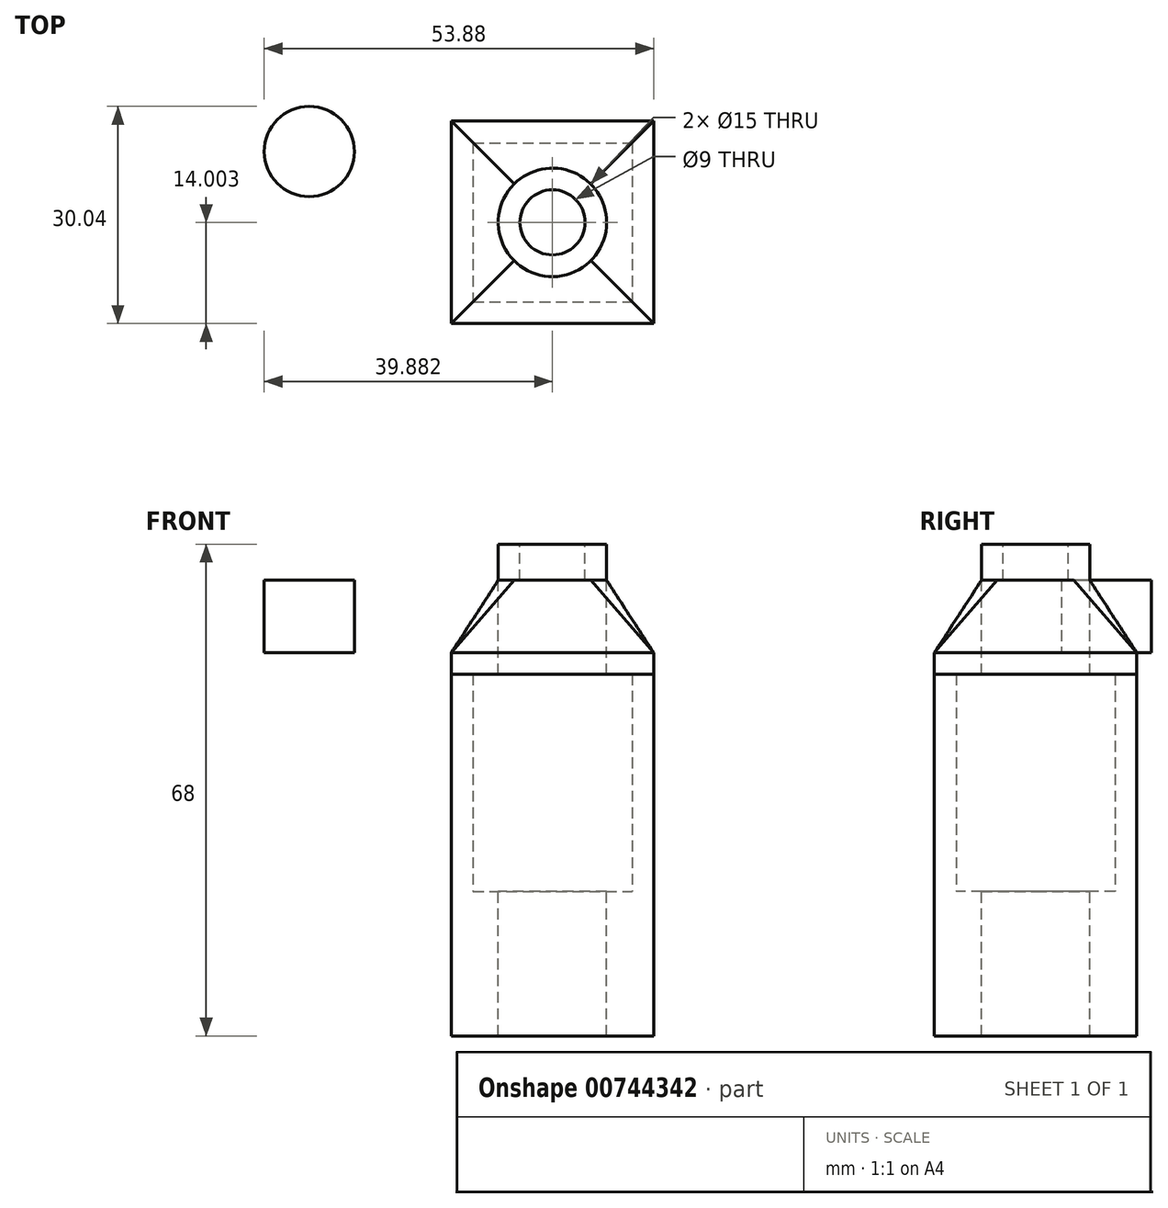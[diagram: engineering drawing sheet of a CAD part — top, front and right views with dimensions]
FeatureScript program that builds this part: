
annotation { "Feature Type Name" : "Feature", "Feature Type Description" : "" }
export const myFeature = defineFeature(function(context is Context, id is Id, definition is map)
    precondition{}
    {
        {
            var Q0;
            Q0=qCreatedBy(makeId("Top.planeOp"),FACE);
            var sketch = newSketch(context, id + "F0", { "sketchPlane" : qUnion([Q0])});
            skLineSegment(sketch, "E0.bottom", {"start": v(-35.87, 27.62) * mm, "end": v(-7.87, 27.62) * mm});
            skLineSegment(sketch, "E0.top", {"start": v(-35.87, -0.38) * mm, "end": v(-7.87, -0.38) * mm});
            skLineSegment(sketch, "E0.left", {"start": v(-35.87, 27.62) * mm, "end": v(-35.87, -0.38) * mm});
            skLineSegment(sketch, "E0.right", {"start": v(-7.87, 27.62) * mm, "end": v(-7.87, -0.38) * mm});
            skLineSegment(sketch, "E1.bottom", {"start": v(-32.87, 24.62) * mm, "end": v(-10.87, 24.62) * mm});
            skLineSegment(sketch, "E1.top", {"start": v(-32.87, 2.62) * mm, "end": v(-10.87, 2.62) * mm});
            skLineSegment(sketch, "E1.left", {"start": v(-32.87, 24.62) * mm, "end": v(-32.87, 2.62) * mm});
            skLineSegment(sketch, "E1.right", {"start": v(-10.87, 24.62) * mm, "end": v(-10.87, 2.62) * mm});
            skSolve(sketch);
        }
        {
            var Q0;
            Q0=makeQuery(id+"F0.imprint","IMPRINT",FACE,{"disambiguationData":[TD([[makeQuery(id+"F0.imprint","IMPRINT",EDGE,{"derivedFrom":sQuery(id+"F0.wireOp",EDGE,"E0.bottom")}),-1.0]])]});
            extrude(context, id + "F1", {"entities" : qUnion([Q0]), "depth" : 50 * mm, "offsetDistance" : 25 * mm});
        }
        {
            var Q0;
            Q0=makeQuery(id+"F0.imprint","IMPRINT",FACE,{"disambiguationData":[TD([[makeQuery(id+"F0.imprint","IMPRINT",EDGE,{"derivedFrom":sQuery(id+"F0.wireOp",EDGE,"E1.bottom")}),-1.0]])]});
            extrude(context, id + "F2", {"entities" : qUnion([Q0]), "operationType" : NewBodyOperationType.ADD, "depth" : 20 * mm, "offsetDistance" : 25 * mm});
        }
        {
            var Q0;
            Q0=makeQuery(id+"F1.opExtrude","CAP_FACE",FACE,{"disambiguationData":[OSD([sQuery(id+"F0.wireOp",EDGE,"E0.bottom"),sQuery(id+"F0.wireOp",EDGE,"E0.top"),sQuery(id+"F0.wireOp",EDGE,"E0.left"),sQuery(id+"F0.wireOp",EDGE,"E0.right"),sQuery(id+"F0.wireOp",EDGE,"E1.bottom"),sQuery(id+"F0.wireOp",EDGE,"E1.top"),sQuery(id+"F0.wireOp",EDGE,"E1.left"),sQuery(id+"F0.wireOp",EDGE,"E1.right")])],"isStart":false});
            var sketch = newSketch(context, id + "F3", { "sketchPlane" : qUnion([Q0])});
            skLineSegment(sketch, "E2.bottom", {"start": v(-35.87, 27.62) * mm, "end": v(-7.87, 27.62) * mm});
            skLineSegment(sketch, "E2.top", {"start": v(-35.87, -0.38) * mm, "end": v(-7.87, -0.38) * mm});
            skLineSegment(sketch, "E2.left", {"start": v(-35.87, 27.62) * mm, "end": v(-35.87, -0.38) * mm});
            skLineSegment(sketch, "E2.right", {"start": v(-7.87, 27.62) * mm, "end": v(-7.87, -0.38) * mm});
            skSolve(sketch);
        }
        {
            var Q0;
            Q0=makeQuery(id+"F3.imprint","IMPRINT",FACE,{"disambiguationData":[TD([[makeQuery(id+"F3.imprint","IMPRINT",EDGE,{"derivedFrom":makeQuery(id+"F1.opExtrude","CAP_EDGE",EDGE,{"disambiguationData":[OSD([sQuery(id+"F0.wireOp",EDGE,"E1.bottom")])],"isStart":false})}),-1.0]])]});
            var Q1;
            Q1=makeQuery(id+"F3.imprint","IMPRINT",FACE,{"disambiguationData":[TD([[makeQuery(id+"F3.imprint","IMPRINT",EDGE,{"derivedFrom":sQuery(id+"F3.wireOp",EDGE,"E2.bottom")}),-1.0]])]});
            extrude(context, id + "F4", {"entities" : qUnion([Q0, Q1]), "depth" : 3 * mm, "offsetDistance" : 25 * mm});
        }
        {
            var Q0;
            Q0=makeQuery(id+"F4.opExtrude","CAP_FACE",FACE,{"disambiguationData":[OSD([sQuery(id+"F3.wireOp",EDGE,"E2.bottom"),sQuery(id+"F3.wireOp",EDGE,"E2.top"),sQuery(id+"F3.wireOp",EDGE,"E2.left"),sQuery(id+"F3.wireOp",EDGE,"E2.right")])],"isStart":false});
            var sketch = newSketch(context, id + "F5", { "sketchPlane" : qUnion([Q0])});
            skCircle(sketch, "E3", {"center": v(-55.52, 23.42) * mm, "radius": 6.24 * mm});
            skSolve(sketch);
        }
        {
            var Q0;
            Q0=makeQuery(id+"F5.imprint","IMPRINT",FACE,{"disambiguationData":[TD([[makeQuery(id+"F5.imprint","IMPRINT",EDGE,{"derivedFrom":sQuery(id+"F5.wireOp",EDGE,"E3")}),1.0]])]});
            extrude(context, id + "F6", {"entities" : qUnion([Q0]), "depth" : 10 * mm, "offsetDistance" : 25 * mm});
        }
        {
            var Q0;
            Q0=makeQuery(id+"F6.opExtrude","CAP_FACE",FACE,{"disambiguationData":[OSD([sQuery(id+"F5.wireOp",EDGE,"E3")])],"isStart":false});
            var sketch = newSketch(context, id + "F7", { "sketchPlane" : qUnion([Q0])});
            skCircle(sketch, "E4", {"center": v(-21.87, 13.62) * mm, "radius": 7.5 * mm});
            skSolve(sketch);
        }
        {
            var Q0;
            Q0=makeQuery(id+"F7.imprint","IMPRINT",FACE,{"disambiguationData":[TD([[makeQuery(id+"F7.imprint","IMPRINT",EDGE,{"derivedFrom":sQuery(id+"F7.wireOp",EDGE,"E4")}),1.0]])]});
            extrude(context, id + "F8", {"entities" : qUnion([Q0]), "depth" : 5 * mm, "offsetDistance" : 25 * mm});
        }
        {
            var Q1;
            Q1=makeQuery(id+"F8.opExtrude","CAP_FACE",FACE,{"disambiguationData":[OSD([sQuery(id+"F7.wireOp",EDGE,"E4")])],"isStart":true});
            var Q2;
            Q2=makeQuery(id+"F4.opExtrude","CAP_FACE",FACE,{"disambiguationData":[OSD([sQuery(id+"F3.wireOp",EDGE,"E2.bottom"),sQuery(id+"F3.wireOp",EDGE,"E2.top"),sQuery(id+"F3.wireOp",EDGE,"E2.left"),sQuery(id+"F3.wireOp",EDGE,"E2.right")])],"isStart":false});
            loft(context, id + "F9", {"operationType" : NewBodyOperationType.ADD, "sheetProfilesArray" : [{ "sheetProfileEntities" : qUnion([Q1]) }, { "sheetProfileEntities" : qUnion([Q2]) }]});
        }
        {
            var Q0;
            Q0=makeQuery(id+"F8.opExtrude","CAP_FACE",FACE,{"disambiguationData":[OSD([sQuery(id+"F7.wireOp",EDGE,"E4")])],"isStart":false});
            var sketch = newSketch(context, id + "F10", { "sketchPlane" : qUnion([Q0])});
            skCircle(sketch, "E5", {"center": v(-21.87, 13.62) * mm, "radius": 4.5 * mm});
            skSolve(sketch);
        }
        {
            var Q0;
            Q0=makeQuery(id+"F10.imprint","IMPRINT",FACE,{"disambiguationData":[TD([[makeQuery(id+"F10.imprint","IMPRINT",EDGE,{"derivedFrom":sQuery(id+"F10.wireOp",EDGE,"E5")}),1.0]])]});
            var Q1;
            Q1 = qSketchRegion(id + "F7", true);
            var Q2;
            Q2 = qSketchRegion(id + "F5", true);
            extrude(context, id + "F11", {"entities" : qUnion([Q0, Q1, Q2]), "operationType" : NewBodyOperationType.REMOVE, "oppositeDirection" : true, "depth" : 200 * mm, "offsetDistance" : 25 * mm});
        }
    });
